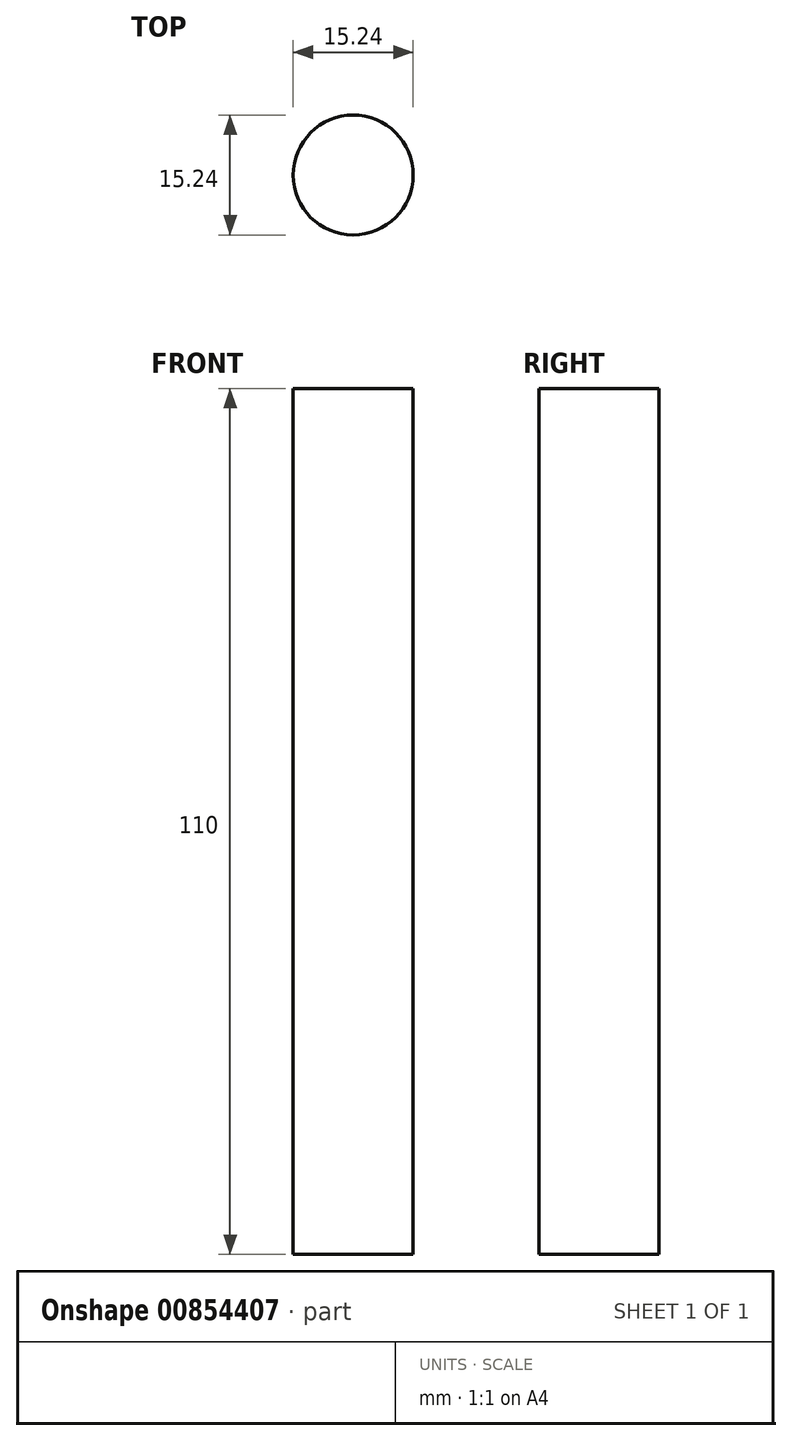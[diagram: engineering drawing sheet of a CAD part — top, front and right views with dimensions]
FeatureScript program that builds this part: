
annotation { "Feature Type Name" : "Feature", "Feature Type Description" : "" }
export const myFeature = defineFeature(function(context is Context, id is Id, definition is map)
    precondition{}
    {
        {
            var Q0;
            Q0=qCreatedBy(makeId("Top.planeOp"),FACE);
            var sketch = newSketch(context, id + "F0", { "sketchPlane" : qUnion([Q0])});
            skCircle(sketch, "E0", {"center": v(0, 0) * mm, "radius": 7.62 * mm});
            skSolve(sketch);
        }
        {
            var Q0;
            Q0 = qSketchRegion(id + "F0", true);
            extrude(context, id + "F1", {"entities" : qUnion([Q0]), "depth" : 110 * mm, "offsetDistance" : 25 * mm});
        }
    });
